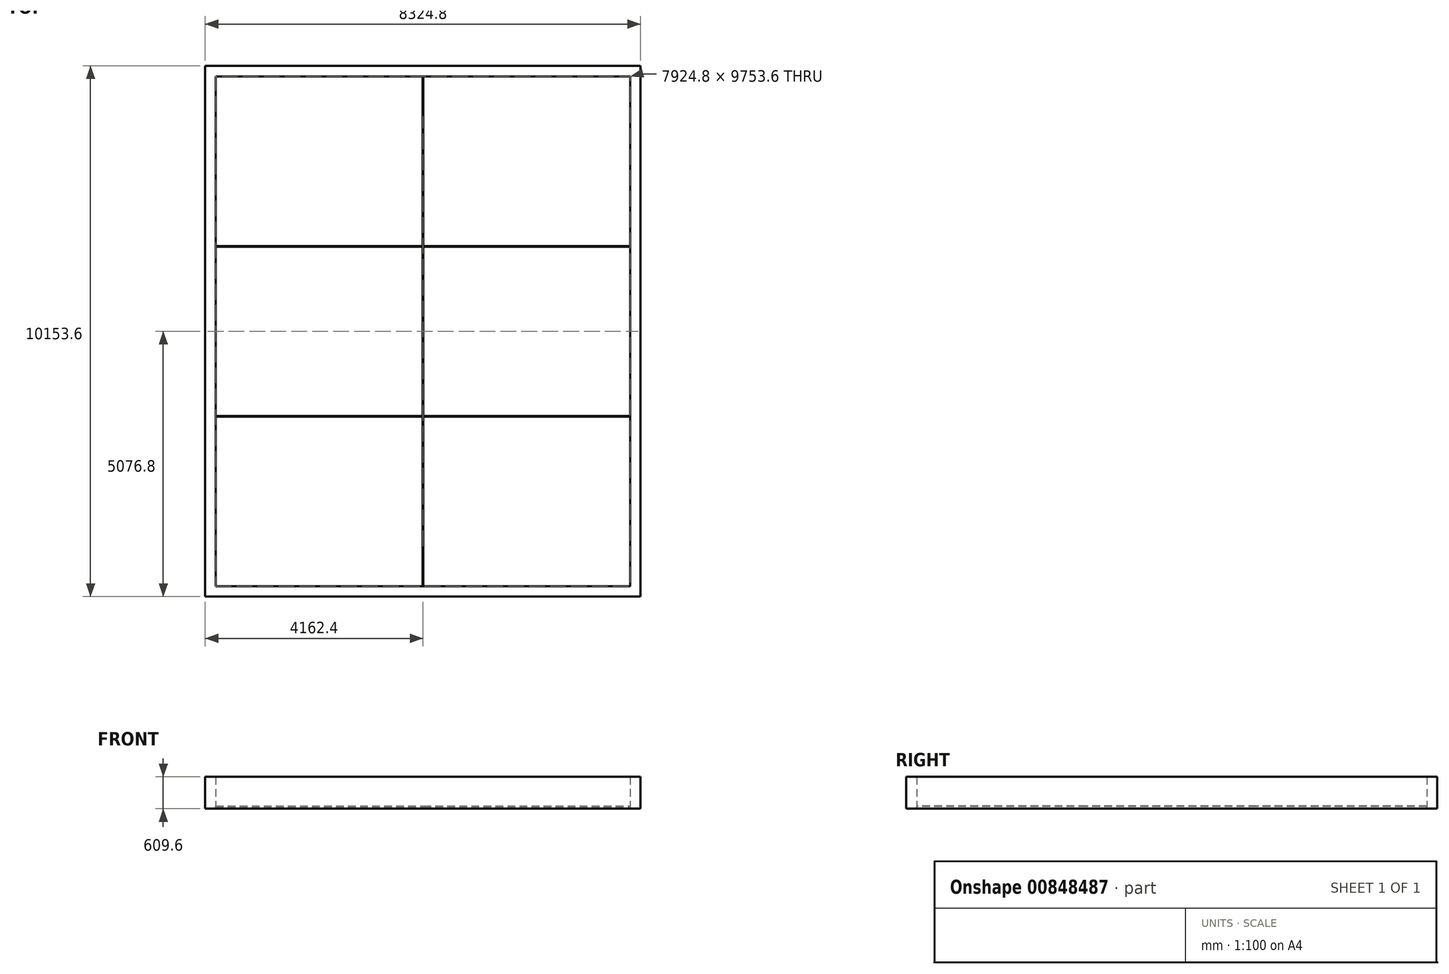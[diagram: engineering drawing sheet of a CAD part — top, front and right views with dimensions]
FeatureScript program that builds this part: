
annotation { "Feature Type Name" : "Feature", "Feature Type Description" : "" }
export const myFeature = defineFeature(function(context is Context, id is Id, definition is map)
    precondition{}
    {
        {
            var Q0;
            Q0=qCreatedBy(makeId("Top.planeOp"),FACE);
            var sketch = newSketch(context, id + "F0", { "sketchPlane" : qUnion([Q0])});
            skLineSegment(sketch, "E0.bottom", {"start": v(-3962.4, 4876.8) * mm, "end": v(3962.4, 4876.8) * mm});
            skLineSegment(sketch, "E0.top", {"start": v(-3962.4, -4876.8) * mm, "end": v(3962.4, -4876.8) * mm});
            skLineSegment(sketch, "E0.left", {"start": v(-3962.4, 4876.8) * mm, "end": v(-3962.4, -4876.8) * mm});
            skLineSegment(sketch, "E0.right", {"start": v(3962.4, 4876.8) * mm, "end": v(3962.4, -4876.8) * mm});
            skPoint(sketch, "E0.middle", {"position": v(0, 0) * mm});
            skSolve(sketch);
        }
        {
            var Q0;
            Q0 = qSketchRegion(id + "F0", true);
            extrude(context, id + "F1", {"entities" : qUnion([Q0]), "oppositeDirection" : true, "depth" : 50.8 * mm, "offsetDistance" : 25.4 * mm});
        }
        {
            var Q0;
            Q0=makeQuery(id+"F1.opExtrude","CAP_FACE",FACE,{"disambiguationData":[OSD([sQuery(id+"F0.wireOp",EDGE,"E0.bottom"),sQuery(id+"F0.wireOp",EDGE,"E0.top"),sQuery(id+"F0.wireOp",EDGE,"E0.left"),sQuery(id+"F0.wireOp",EDGE,"E0.right")])],"isStart":true});
            var sketch = newSketch(context, id + "F2", { "sketchPlane" : qUnion([Q0])});
            skLineSegment(sketch, "E1.bottom", {"start": v(-3962.4, -1631.95) * mm, "end": v(-6.35, -1631.95) * mm});
            skLineSegment(sketch, "E1.top", {"start": v(-3962.4, -1619.25) * mm, "end": v(-6.35, -1619.25) * mm});
            skLineSegment(sketch, "E1.left", {"start": v(-3962.4, -1631.95) * mm, "end": v(-3962.4, -1619.25) * mm});
            skLineSegment(sketch, "E1.right", {"start": v(3962.4, -1631.95) * mm, "end": v(3962.4, -1619.25) * mm});
            skLineSegment(sketch, "E2.0.1.0", {"start": v(-3962.4, 1619.25) * mm, "end": v(-6.35, 1619.25) * mm});
            skLineSegment(sketch, "E2.0.1.1", {"start": v(-3962.4, 1631.95) * mm, "end": v(-6.35, 1631.95) * mm});
            skLineSegment(sketch, "E2.0.1.2", {"start": v(3962.4, 1619.25) * mm, "end": v(3962.4, 1631.95) * mm});
            skLineSegment(sketch, "E2.0.1.3", {"start": v(-3962.4, 1619.25) * mm, "end": v(-3962.4, 1631.95) * mm});
            skLineSegment(sketch, "E2.direction1", {"start": v(-3962.4, -1631.95) * mm, "end": v(-3937, -1631.95) * mm, "construction": true});
            skLineSegment(sketch, "E2.direction2", {"start": v(-3962.4, -1631.95) * mm, "end": v(-3962.4, 1619.25) * mm, "construction": true});
            skLineSegment(sketch, "E3.bottom", {"start": v(-6.35, 4876.8) * mm, "end": v(6.35, 4876.8) * mm});
            skLineSegment(sketch, "E3.top", {"start": v(-6.35, -4876.8) * mm, "end": v(6.35, -4876.8) * mm});
            skLineSegment(sketch, "E4.trimOffspring", {"start": v(6.35, 4876.8) * mm, "end": v(6.35, 1631.95) * mm});
            skLineSegment(sketch, "E5.trimOffspring", {"start": v(-6.35, 4876.8) * mm, "end": v(-6.35, 1631.95) * mm});
            skLineSegment(sketch, "E6.trimOffspring", {"start": v(6.35, 1631.95) * mm, "end": v(3962.4, 1631.95) * mm});
            skLineSegment(sketch, "E7.trimOffspring", {"start": v(-6.35, 1619.25) * mm, "end": v(-6.35, -1619.25) * mm});
            skLineSegment(sketch, "E8.trimOffspring", {"start": v(6.35, 1619.25) * mm, "end": v(6.35, -1619.25) * mm});
            skLineSegment(sketch, "E9.trimOffspring", {"start": v(6.35, 1619.25) * mm, "end": v(3962.4, 1619.25) * mm});
            skLineSegment(sketch, "E10.trimOffspring", {"start": v(6.35, -1631.95) * mm, "end": v(3962.4, -1631.95) * mm});
            skLineSegment(sketch, "E11.trimOffspring", {"start": v(-6.35, -1631.95) * mm, "end": v(-6.35, -4876.8) * mm});
            skLineSegment(sketch, "E12.trimOffspring", {"start": v(6.35, -1619.25) * mm, "end": v(3962.4, -1619.25) * mm});
            skLineSegment(sketch, "E13.trimOffspring", {"start": v(6.35, -1631.95) * mm, "end": v(6.35, -4876.8) * mm});
            skSolve(sketch);
        }
        {
            var Q0;
            Q0 = qSketchRegion(id + "F2", true);
            extrude(context, id + "F3", {"entities" : qUnion([Q0]), "operationType" : NewBodyOperationType.REMOVE, "oppositeDirection" : true, "depth" : 12.7 * mm, "offsetDistance" : 25.4 * mm});
        }
        {
            var Q0;
            Q0=makeQuery(id+"F1.opExtrude","CAP_FACE",FACE,{"disambiguationData":[OSD([sQuery(id+"F0.wireOp",EDGE,"E0.bottom"),sQuery(id+"F0.wireOp",EDGE,"E0.top"),sQuery(id+"F0.wireOp",EDGE,"E0.left"),sQuery(id+"F0.wireOp",EDGE,"E0.right")])],"isStart":false});
            var sketch = newSketch(context, id + "F4", { "sketchPlane" : qUnion([Q0])});
            skLineSegment(sketch, "E14.right", {"start": v(-4162.4, 5076.8) * mm, "end": v(-4162.4, -5076.8) * mm});
            skLineSegment(sketch, "E15.bottom", {"start": v(-4162.4, -5076.8) * mm, "end": v(4162.4, -5076.8) * mm});
            skLineSegment(sketch, "E15.top", {"start": v(-3962.4, -4876.8) * mm, "end": v(3962.4, -4876.8) * mm});
            skLineSegment(sketch, "E16.left", {"start": v(4162.4, -5076.8) * mm, "end": v(4162.4, 5076.8) * mm});
            skLineSegment(sketch, "E16.right", {"start": v(3962.4, -4876.8) * mm, "end": v(3962.4, 4876.8) * mm});
            skLineSegment(sketch, "E17.bottom", {"start": v(4162.4, 5076.8) * mm, "end": v(-4162.4, 5076.8) * mm});
            skLineSegment(sketch, "E17.top", {"start": v(3962.4, 4876.8) * mm, "end": v(-3962.4, 4876.8) * mm});
            skLineSegment(sketch, "E18.trimOffspring", {"start": v(-3962.4, 4876.8) * mm, "end": v(-3962.4, -4876.8) * mm});
            skSolve(sketch);
        }
        {
            var Q0;
            Q0 = qSketchRegion(id + "F4", true);
            extrude(context, id + "F5", {"entities" : qUnion([Q0]), "oppositeDirection" : true, "depth" : 609.6 * mm, "offsetDistance" : 25.4 * mm});
        }
    });
